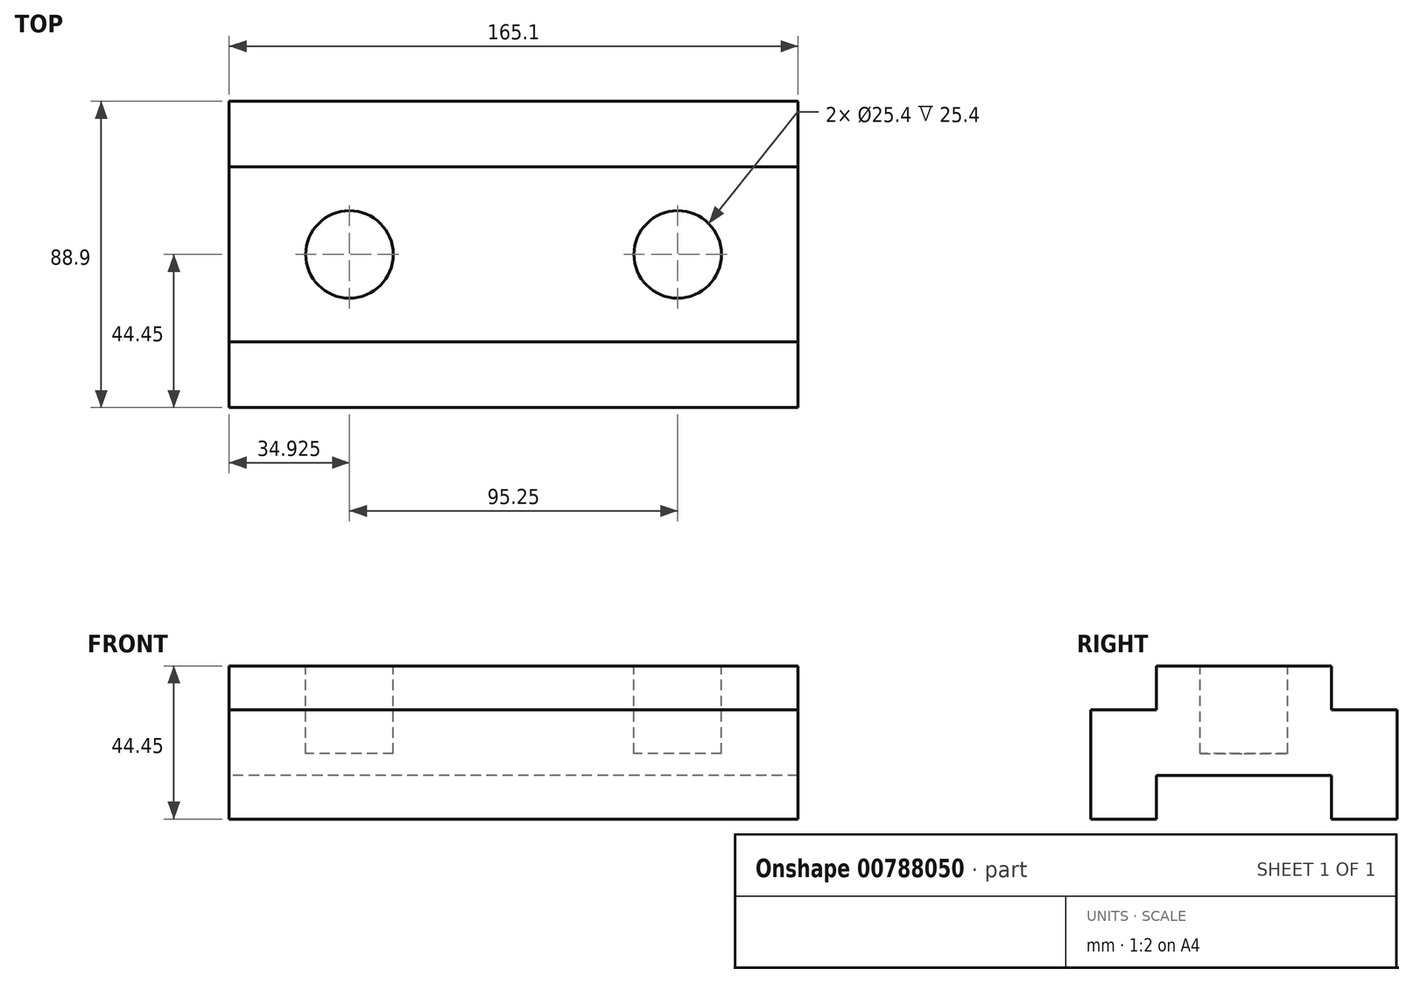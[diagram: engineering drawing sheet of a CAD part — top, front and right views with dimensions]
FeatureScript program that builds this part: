
annotation { "Feature Type Name" : "Feature", "Feature Type Description" : "" }
export const myFeature = defineFeature(function(context is Context, id is Id, definition is map)
    precondition{}
    {
        {
            var Q0;
            Q0=qCreatedBy(makeId("Right.planeOp"),FACE);
            var sketch = newSketch(context, id + "F0", { "sketchPlane" : qUnion([Q0])});
            skLineSegment(sketch, "E0", {"start": v(0, 0) * mm, "end": v(19.05, 0) * mm});
            skLineSegment(sketch, "E1", {"start": v(19.05, 0) * mm, "end": v(19.05, 12.7) * mm});
            skLineSegment(sketch, "E2", {"start": v(19.05, 12.7) * mm, "end": v(69.85, 12.7) * mm});
            skLineSegment(sketch, "E3", {"start": v(69.85, 12.7) * mm, "end": v(69.85, 0) * mm});
            skLineSegment(sketch, "E4", {"start": v(69.85, 0) * mm, "end": v(88.9, 0) * mm});
            skLineSegment(sketch, "E5", {"start": v(88.9, 0) * mm, "end": v(88.9, 31.75) * mm});
            skLineSegment(sketch, "E6", {"start": v(88.9, 31.75) * mm, "end": v(69.85, 31.75) * mm});
            skLineSegment(sketch, "E7", {"start": v(69.85, 31.75) * mm, "end": v(69.85, 44.45) * mm});
            skLineSegment(sketch, "E8", {"start": v(19.05, 44.45) * mm, "end": v(69.85, 44.45) * mm});
            skLineSegment(sketch, "E9", {"start": v(19.05, 44.45) * mm, "end": v(19.05, 31.75) * mm});
            skLineSegment(sketch, "E10", {"start": v(19.05, 31.75) * mm, "end": v(0, 31.75) * mm});
            skLineSegment(sketch, "E11", {"start": v(0, 31.75) * mm, "end": v(0, 0) * mm});
            skSolve(sketch);
        }
        {
            var Q0;
            Q0=makeQuery(id+"F0.imprint","IMPRINT",FACE,{"disambiguationData":[TD([[makeQuery(id+"F0.imprint","IMPRINT",EDGE,{"derivedFrom":sQuery(id+"F0.wireOp",EDGE,"E0")}),1.0]])]});
            extrude(context, id + "F1", {"entities" : qUnion([Q0]), "depth" : 165.1 * mm, "offsetDistance" : 25.4 * mm});
        }
        {
            var Q0;
            Q0=makeQuery(id+"F1.opExtrude","SWEPT_FACE",FACE,{"disambiguationData":[OSD([sQuery(id+"F0.wireOp",EDGE,"E8")])]});
            var sketch = newSketch(context, id + "F2", { "sketchPlane" : qUnion([Q0])});
            skLineSegment(sketch, "E12", {"start": v(0, 44.45) * mm, "end": v(34.93, 44.45) * mm, "construction": true});
            skLineSegment(sketch, "E13", {"start": v(34.93, 44.45) * mm, "end": v(130.18, 44.45) * mm, "construction": true});
            skCircle(sketch, "E14", {"center": v(34.93, 44.45) * mm, "radius": 12.7 * mm});
            skCircle(sketch, "E15", {"center": v(130.18, 44.45) * mm, "radius": 12.7 * mm});
            skSolve(sketch);
        }
        {
            var Q0;
            Q0=makeQuery(id+"F2.imprint","IMPRINT",FACE,{"disambiguationData":[TD([[makeQuery(id+"F2.imprint","IMPRINT",EDGE,{"derivedFrom":sQuery(id+"F2.wireOp",EDGE,"E14")}),1.0]])]});
            var Q1;
            Q1=makeQuery(id+"F2.imprint","IMPRINT",FACE,{"disambiguationData":[TD([[makeQuery(id+"F2.imprint","IMPRINT",EDGE,{"derivedFrom":sQuery(id+"F2.wireOp",EDGE,"E15")}),1.0]])]});
            extrude(context, id + "F3", {"entities" : qUnion([Q0, Q1]), "operationType" : NewBodyOperationType.REMOVE, "oppositeDirection" : true, "depth" : 25.4 * mm, "offsetDistance" : 25.4 * mm});
        }
    });
